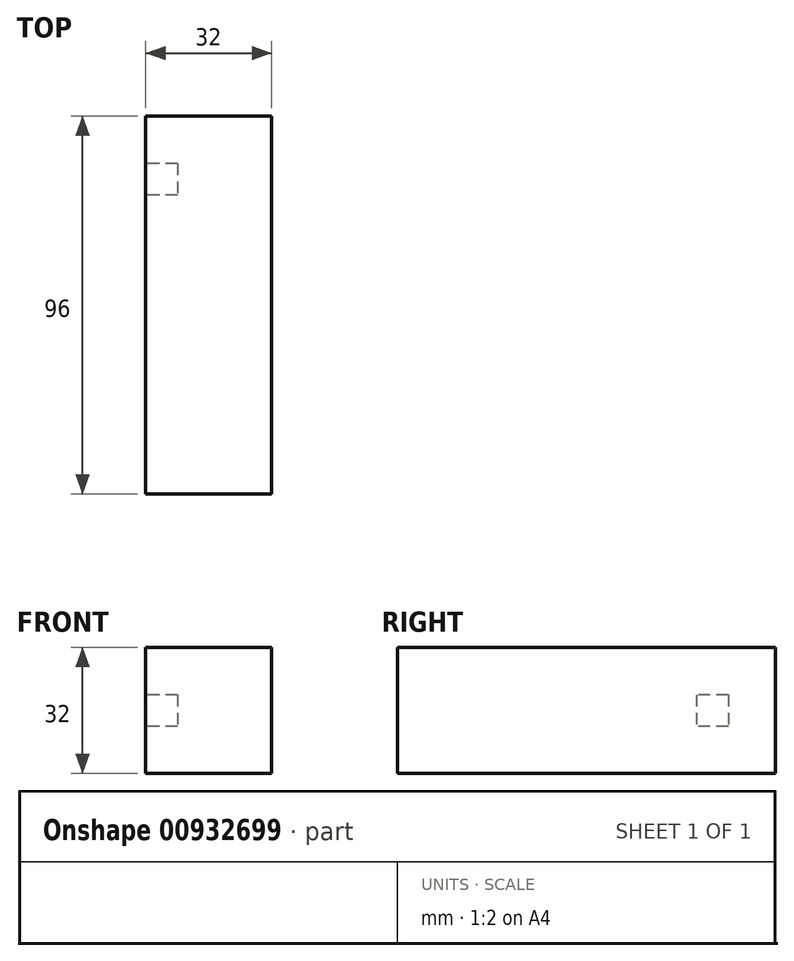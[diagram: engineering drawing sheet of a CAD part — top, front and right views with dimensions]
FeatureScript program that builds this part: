
annotation { "Feature Type Name" : "Feature", "Feature Type Description" : "" }
export const myFeature = defineFeature(function(context is Context, id is Id, definition is map)
    precondition{}
    {
        {
            var Q0;
            Q0=qCreatedBy(makeId("Top.planeOp"),FACE);
            var sketch = newSketch(context, id + "F0", { "sketchPlane" : qUnion([Q0])});
            skLineSegment(sketch, "E0.bottom", {"start": v(-16, 48) * mm, "end": v(16, 48) * mm});
            skLineSegment(sketch, "E0.top", {"start": v(-16, -48) * mm, "end": v(16, -48) * mm});
            skLineSegment(sketch, "E0.left", {"start": v(-16, 48) * mm, "end": v(-16, -48) * mm});
            skLineSegment(sketch, "E0.right", {"start": v(16, 48) * mm, "end": v(16, -48) * mm});
            skSolve(sketch);
        }
        {
            var Q0;
            Q0=qSketchRegion(id+"F0",true);
            extrude(context, id + "F1", {"entities" : qUnion([Q0]), "depth" : 32 * mm, "offsetDistance" : 25 * mm});
        }
        {
            var Q0;
            Q0=makeQuery(id+"F1.opExtrude","SWEPT_FACE",FACE,{"disambiguationData":[OSD([sQuery(id+"F0.wireOp",EDGE,"E0.left")])]});
            var sketch = newSketch(context, id + "F2", { "sketchPlane" : qUnion([Q0])});
            skLineSegment(sketch, "E1.bottom", {"start": v(-36, 20) * mm, "end": v(-27.9, 20) * mm});
            skLineSegment(sketch, "E1.top", {"start": v(-36, 11.9) * mm, "end": v(-27.9, 11.9) * mm});
            skLineSegment(sketch, "E1.left", {"start": v(-36, 20) * mm, "end": v(-36, 11.9) * mm});
            skLineSegment(sketch, "E1.right", {"start": v(-27.9, 20) * mm, "end": v(-27.9, 11.9) * mm});
            skSolve(sketch);
        }
        {
            var Q0;
            Q0 = qSketchRegion(id + "F2", true);
            extrude(context, id + "F3", {"entities" : qUnion([Q0]), "operationType" : NewBodyOperationType.REMOVE, "oppositeDirection" : true, "depth" : 8.1 * mm, "offsetDistance" : 25 * mm});
        }
    });
